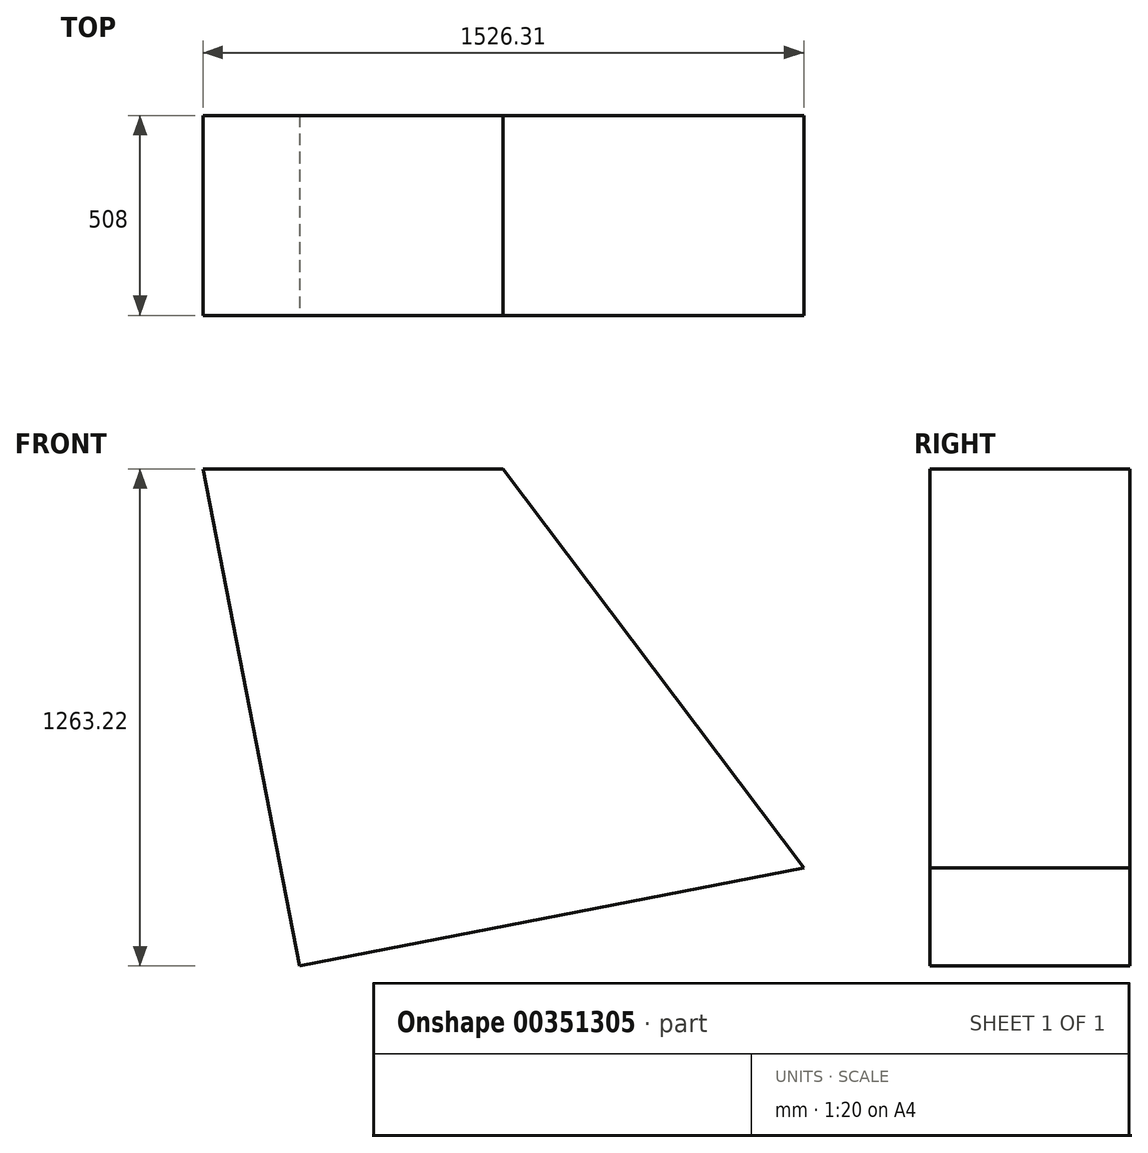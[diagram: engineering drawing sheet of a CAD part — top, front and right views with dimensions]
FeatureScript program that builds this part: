
annotation { "Feature Type Name" : "Feature", "Feature Type Description" : "" }
export const myFeature = defineFeature(function(context is Context, id is Id, definition is map)
    precondition{}
    {
        {
            var Q0;
            Q0=qCreatedBy(makeId("Front.planeOp"),FACE);
            var sketch = newSketch(context, id + "F0", { "sketchPlane" : qUnion([Q0])});
            skLineSegment(sketch, "E0", {"start": v(0, 0) * mm, "end": v(762, 0) * mm});
            skLineSegment(sketch, "E1", {"start": v(762, 0) * mm, "end": v(1526.3, -1014.27) * mm});
            skLineSegment(sketch, "E2", {"start": v(1526.3, -1014.27) * mm, "end": v(245.55, -1263.22) * mm});
            skLineSegment(sketch, "E3", {"start": v(245.55, -1263.22) * mm, "end": v(0, 0) * mm});
            skSolve(sketch);
        }
        {
            var Q0;
            Q0=makeQuery(id+"F0.imprint","IMPRINT",FACE,{"disambiguationData":[TD([[makeQuery(id+"F0.imprint","IMPRINT",EDGE,{"derivedFrom":sQuery(id+"F0.wireOp",EDGE,"E0")}),-1.0]])]});
            extrude(context, id + "F1", {"entities" : qUnion([Q0]), "oppositeDirection" : true, "depth" : 508 * mm});
        }
    });
